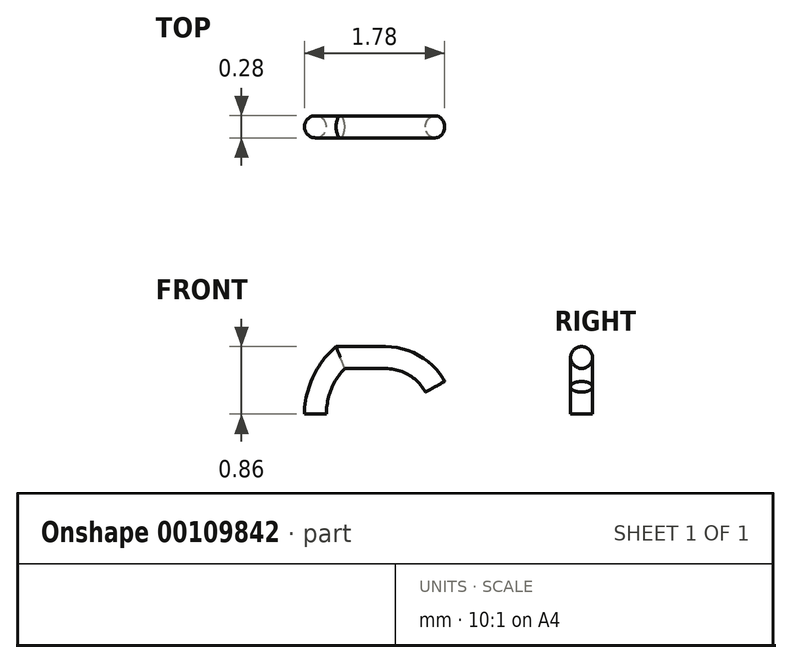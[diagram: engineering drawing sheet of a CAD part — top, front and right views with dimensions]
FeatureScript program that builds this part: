
annotation { "Feature Type Name" : "Feature", "Feature Type Description" : "" }
export const myFeature = defineFeature(function(context is Context, id is Id, definition is map)
    precondition{}
    {
        {
            var Q0;
            Q0=qCreatedBy(makeId("Top.planeOp"),FACE);
            var sketch = newSketch(context, id + "F0", { "sketchPlane" : qUnion([Q0])});
            skCircle(sketch, "E0", {"center": v(0, 0) * mm, "radius": 0.14 * mm});
            skSolve(sketch);
        }
        {
            var Q0;
            Q0=qCreatedBy(makeId("Front.planeOp"),FACE);
            var sketch = newSketch(context, id + "F1", { "sketchPlane" : qUnion([Q0])});
            skArc(sketch, "E1", {"start": v(0, 0) * mm, "mid": v(0.08, 0.4) * mm, "end": v(0.32, 0.72) * mm});
            skLineSegment(sketch, "E2", {"start": v(0.32, 0.72) * mm, "end": v(0.9, 0.72) * mm});
            skArc(sketch, "E3", {"start": v(0.9, 0.72) * mm, "mid": v(1.26, 0.62) * mm, "end": v(1.52, 0.35) * mm});
            skSolve(sketch);
        }
        {
            var Q0;
            Q0 = qSketchRegion(id + "F0", true);
            var Q1;
            Q1 = qConstructionFilter(qBodyType(qCreatedBy(id + "F1" ,EDGE), BodyType.WIRE), ConstructionObject.NO);
            sweep(context, id + "F2", {"profiles" : qUnion([Q0]), "path" : qUnion([Q1])});
        }
    });
